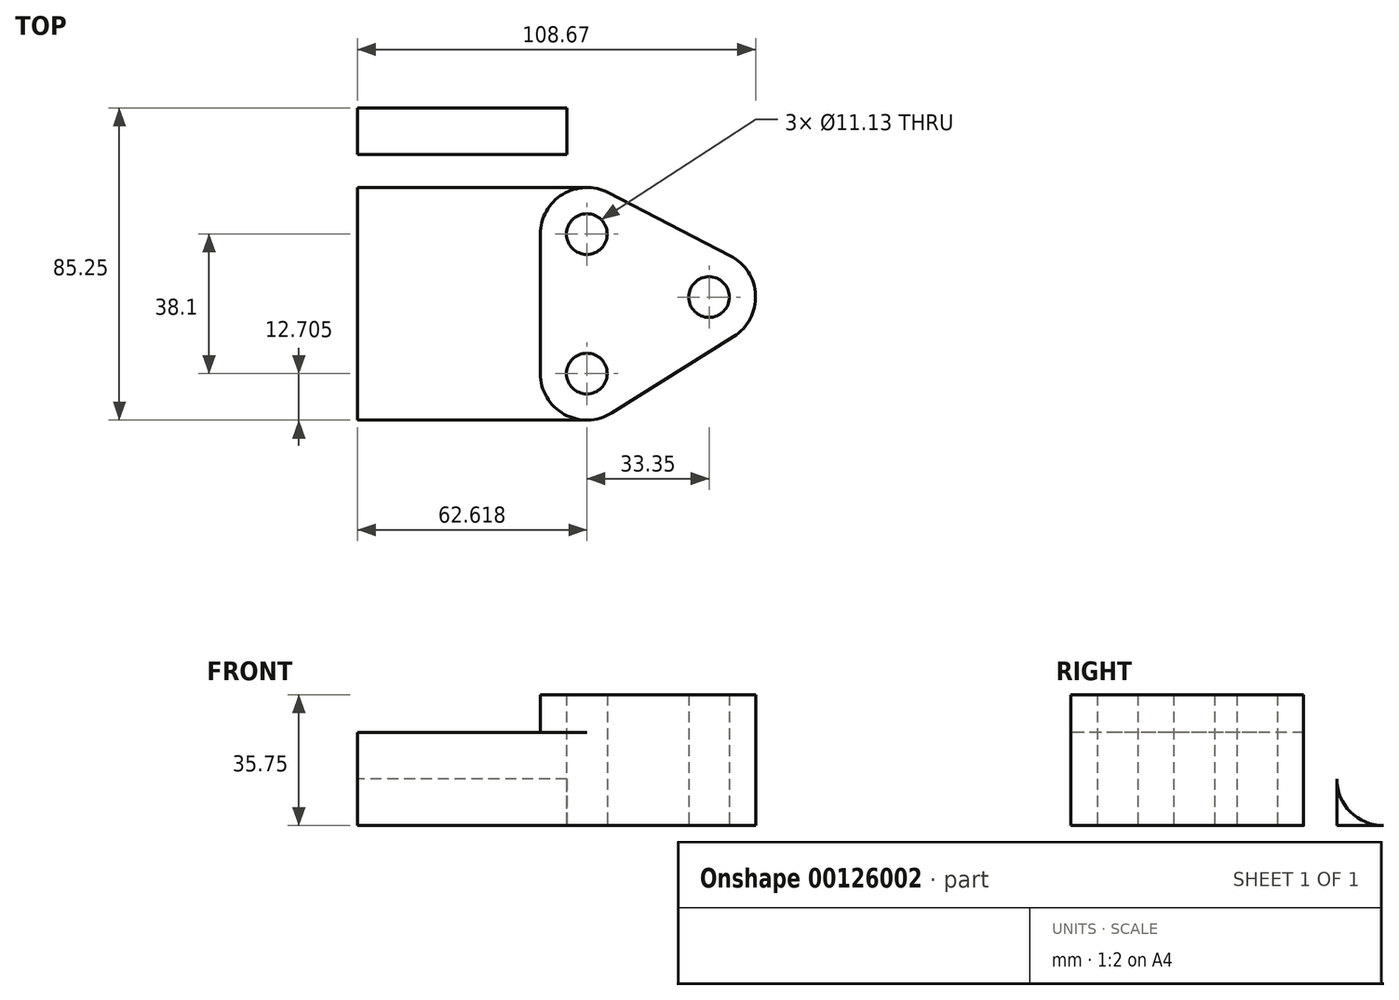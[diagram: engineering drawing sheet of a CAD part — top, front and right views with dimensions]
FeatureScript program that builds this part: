
annotation { "Feature Type Name" : "Feature", "Feature Type Description" : "" }
export const myFeature = defineFeature(function(context is Context, id is Id, definition is map)
    precondition{}
    {
        {
            var Q0;
            Q0=qCreatedBy(makeId("Top.planeOp"),FACE);
            var sketch = newSketch(context, id + "F0", { "sketchPlane" : qUnion([Q0])});
            skLineSegment(sketch, "E0", {"start": v(0, 0) * mm, "end": v(0, 88.9) * mm});
            skLineSegment(sketch, "E1", {"start": v(0, 0) * mm, "end": v(57.15, 0) * mm});
            skLineSegment(sketch, "E2", {"start": v(57.15, 0) * mm, "end": v(57.15, 15.87) * mm});
            skLineSegment(sketch, "E3", {"start": v(63.5, 66.68) * mm, "end": v(111.12, 66.68) * mm});
            skLineSegment(sketch, "E4", {"start": v(63.5, 22.23) * mm, "end": v(111.12, 22.23) * mm});
            skArc(sketch, "E5", {"start": v(111.12, 66.68) * mm, "mid": v(133.35, 44.45) * mm, "end": v(111.12, 22.23) * mm});
            skCircle(sketch, "E6", {"center": v(111.12, 44.45) * mm, "radius": 10.33 * mm});
            skCircle(sketch, "E7", {"center": v(73.03, 44.45) * mm, "radius": 10.33 * mm});
            skArc(sketch, "E8", {"start": v(57.15, 15.87) * mm, "mid": v(59, 20.37) * mm, "end": v(63.5, 22.23) * mm});
            skLineSegment(sketch, "E9", {"start": v(0, 88.9) * mm, "end": v(57.15, 88.9) * mm});
            skLineSegment(sketch, "E10", {"start": v(57.15, 88.9) * mm, "end": v(57.15, 73.03) * mm});
            skArc(sketch, "E11", {"start": v(57.15, 73.03) * mm, "mid": v(59, 68.53) * mm, "end": v(63.5, 66.68) * mm});
            skSolve(sketch);
        }
        {
            var Q0;
            Q0 = qSketchRegion(id + "F0", true);
            extrude(context, id + "F1", {"entities" : qUnion([Q0]), "depth" : 73.02 * mm});
        }
        {
            var Q0;
            Q0=makeQuery(id+"F1.opExtrude","SWEPT_FACE",FACE,{"disambiguationData":[OSD([sQuery(id+"F0.wireOp",EDGE,"E0")])]});
            var sketch = newSketch(context, id + "F2", { "sketchPlane" : qUnion([Q0])});
            skLineSegment(sketch, "E12", {"start": v(-88.9, 73.03) * mm, "end": v(-88.9, 12.7) * mm});
            skLineSegment(sketch, "E13", {"start": v(-76.2, 0) * mm, "end": v(-12.7, 0) * mm});
            skLineSegment(sketch, "E14", {"start": v(0, 12.7) * mm, "end": v(0, 73.03) * mm});
            skLineSegment(sketch, "E15", {"start": v(0, 73.03) * mm, "end": v(-7.94, 73.03) * mm});
            skLineSegment(sketch, "E16", {"start": v(-7.94, 73.03) * mm, "end": v(-7.94, 12.7) * mm});
            skLineSegment(sketch, "E17", {"start": v(-12.7, 7.94) * mm, "end": v(-76.2, 7.94) * mm});
            skLineSegment(sketch, "E18", {"start": v(-80.96, 12.7) * mm, "end": v(-80.96, 73.03) * mm});
            skLineSegment(sketch, "E19", {"start": v(-80.96, 73.03) * mm, "end": v(-88.9, 73.03) * mm});
            skArc(sketch, "E20", {"start": v(-88.9, 12.7) * mm, "mid": v(-85.18, 3.72) * mm, "end": v(-76.2, 0) * mm});
            skArc(sketch, "E21", {"start": v(0, 12.7) * mm, "mid": v(-3.72, 3.72) * mm, "end": v(-12.7, 0) * mm});
            skArc(sketch, "E22", {"start": v(-80.96, 12.7) * mm, "mid": v(-79.57, 9.33) * mm, "end": v(-76.2, 7.94) * mm});
            skArc(sketch, "E23", {"start": v(-7.94, 12.7) * mm, "mid": v(-9.33, 9.33) * mm, "end": v(-12.7, 7.94) * mm});
            skSolve(sketch);
        }
        {
            var Q0;
            {var subQ0=sQuery(id+"F2.wireOp",EDGE,"E16");Q0=makeQuery(id+"F2.imprint","IMPRINT",FACE,{"disambiguationData":[TD([[makeQuery(id+"F2.imprint","IMPRINT",EDGE,{"derivedFrom":subQ0}),-1.0]])]});}
            var Q1;
            {var subQ0=sQuery(id+"F2.wireOp",EDGE,"E20");Q1=makeQuery(id+"F2.imprint","IMPRINT",FACE,{"disambiguationData":[TD([[makeQuery(id+"F2.imprint","IMPRINT",EDGE,{"derivedFrom":subQ0}),-1.0]])]});}
            var Q2;
            {var subQ0=sQuery(id+"F2.wireOp",EDGE,"E21");Q2=makeQuery(id+"F2.imprint","IMPRINT",FACE,{"disambiguationData":[TD([[makeQuery(id+"F2.imprint","IMPRINT",EDGE,{"derivedFrom":subQ0}),1.0]])]});}
            extrude(context, id + "F3", {"entities" : qUnion([Q0, Q1, Q2]), "operationType" : NewBodyOperationType.REMOVE, "endBound" : BoundingType.THROUGH_ALL, "oppositeDirection" : true, "depth" : 25.4 * mm});
        }
        {
            var Q0;
            Q0=makeQuery(id+"F1.opExtrude","SWEPT_FACE",FACE,{"disambiguationData":[OSD([sQuery(id+"F0.wireOp",EDGE,"E1")])]});
            var sketch = newSketch(context, id + "F4", { "sketchPlane" : qUnion([Q0])});
            skLineSegment(sketch, "E24", {"start": v(0, 12.7) * mm, "end": v(0, 44.45) * mm});
            skLineSegment(sketch, "E25", {"start": v(57.15, 44.45) * mm, "end": v(57.15, 12.7) * mm});
            skArc(sketch, "E26", {"start": v(0, 44.45) * mm, "mid": v(28.58, 73.03) * mm, "end": v(57.15, 44.45) * mm});
            skCircle(sketch, "E27", {"center": v(28.58, 44.45) * mm, "radius": 9.92 * mm});
            skSolve(sketch);
        }
        {
            var Q0;
            Q0=makeQuery(id+"F4.imprint","IMPRINT",FACE,{"disambiguationData":[TD([[makeQuery(id+"F4.imprint","IMPRINT",EDGE,{"derivedFrom":sQuery(id+"F4.wireOp",EDGE,"E27")}),1.0]])]});
            var Q1;
            {var subQ0=sQuery(id+"F4.wireOp",EDGE,"E26");var subQ1=sQuery(id+"F0.wireOp",EDGE,"E1");var subQ4=makeQuery(id+"F1.opExtrude","CAP_EDGE",EDGE,{"disambiguationData":[OSD([subQ1])],"isStart":false});var subQ5=makeQuery(id+"F4.imprint","INTERSECT",VERTEX,{"derivedFrom":[subQ4,subQ0]});Q1=makeQuery(id+"F4.imprint","IMPRINT",FACE,{"disambiguationData":[TD([[makeQuery(id+"F4.imprint","IMPRINT",EDGE,{"disambiguationData":[TD([[subQ5,-1.0]])],"derivedFrom":subQ4}),-1.0]])]});}
            var Q2;
            {var subQ0=sQuery(id+"F4.wireOp",EDGE,"E26");var subQ1=sQuery(id+"F0.wireOp",EDGE,"E1");var subQ4=makeQuery(id+"F1.opExtrude","CAP_EDGE",EDGE,{"disambiguationData":[OSD([subQ1])],"isStart":false});var subQ5=makeQuery(id+"F4.imprint","INTERSECT",VERTEX,{"derivedFrom":[subQ4,subQ0]});Q2=makeQuery(id+"F4.imprint","IMPRINT",FACE,{"disambiguationData":[TD([[makeQuery(id+"F4.imprint","IMPRINT",EDGE,{"disambiguationData":[TD([[subQ5,1.0]])],"derivedFrom":subQ4}),-1.0]])]});}
            extrude(context, id + "F5", {"entities" : qUnion([Q0, Q1, Q2]), "operationType" : NewBodyOperationType.REMOVE, "endBound" : BoundingType.THROUGH_ALL, "oppositeDirection" : true, "depth" : 25.4 * mm});
        }
        {
            var Q0;
            Q0=qCreatedBy(makeId("Top.planeOp"),FACE);
            var sketch = newSketch(context, id + "F6", { "sketchPlane" : qUnion([Q0])});
            skLineSegment(sketch, "E28", {"start": v(0, -9.05) * mm, "end": v(0, -72.55) * mm});
            skLineSegment(sketch, "E29", {"start": v(0, -72.55) * mm, "end": v(62.62, -72.55) * mm});
            skLineSegment(sketch, "E30", {"start": v(62.62, -9.05) * mm, "end": v(0, -9.05) * mm});
            skLineSegment(sketch, "E31", {"start": v(49.92, -21.75) * mm, "end": v(49.92, -59.85) * mm});
            skLineSegment(sketch, "E32", {"start": v(68.44, -10.46) * mm, "end": v(101.8, -27.68) * mm});
            skLineSegment(sketch, "E33", {"start": v(69.36, -70.6) * mm, "end": v(102.7, -49.73) * mm});
            skArc(sketch, "E34", {"start": v(49.92, -21.75) * mm, "mid": v(56.01, -10.9) * mm, "end": v(68.44, -10.46) * mm});
            skArc(sketch, "E35", {"start": v(49.92, -59.85) * mm, "mid": v(56.47, -70.96) * mm, "end": v(69.36, -70.6) * mm});
            skArc(sketch, "E36", {"start": v(101.8, -27.68) * mm, "mid": v(108.66, -38.44) * mm, "end": v(102.7, -49.73) * mm});
            skCircle(sketch, "E37", {"center": v(62.62, -59.85) * mm, "radius": 5.56 * mm});
            skCircle(sketch, "E38", {"center": v(95.97, -38.96) * mm, "radius": 5.56 * mm});
            skCircle(sketch, "E39", {"center": v(62.62, -21.75) * mm, "radius": 5.56 * mm});
            skLineSegment(sketch, "E40", {"start": v(25.34, -9.05) * mm, "end": v(25.34, -72.55) * mm, "construction": true});
            skSolve(sketch);
        }
        {
            var Q0;
            Q0=makeQuery(id+"F6.imprint","IMPRINT",FACE,{"disambiguationData":[TD([[makeQuery(id+"F6.imprint","IMPRINT",EDGE,{"derivedFrom":sQuery(id+"F6.wireOp",EDGE,"E28")}),1.0]])]});
            extrude(context, id + "F7", {"entities" : qUnion([Q0]), "depth" : 25.4 * mm});
        }
        {
            var Q0;
            {var subQ4=sQuery(id+"F6.wireOp",EDGE,"E31");Q0=makeQuery(id+"F6.imprint","IMPRINT",FACE,{"disambiguationData":[TD([[makeQuery(id+"F6.imprint","IMPRINT",EDGE,{"derivedFrom":subQ4}),1.0]])]});}
            extrude(context, id + "F8", {"entities" : qUnion([Q0]), "operationType" : NewBodyOperationType.ADD, "depth" : 35.75 * mm});
        }
    });
